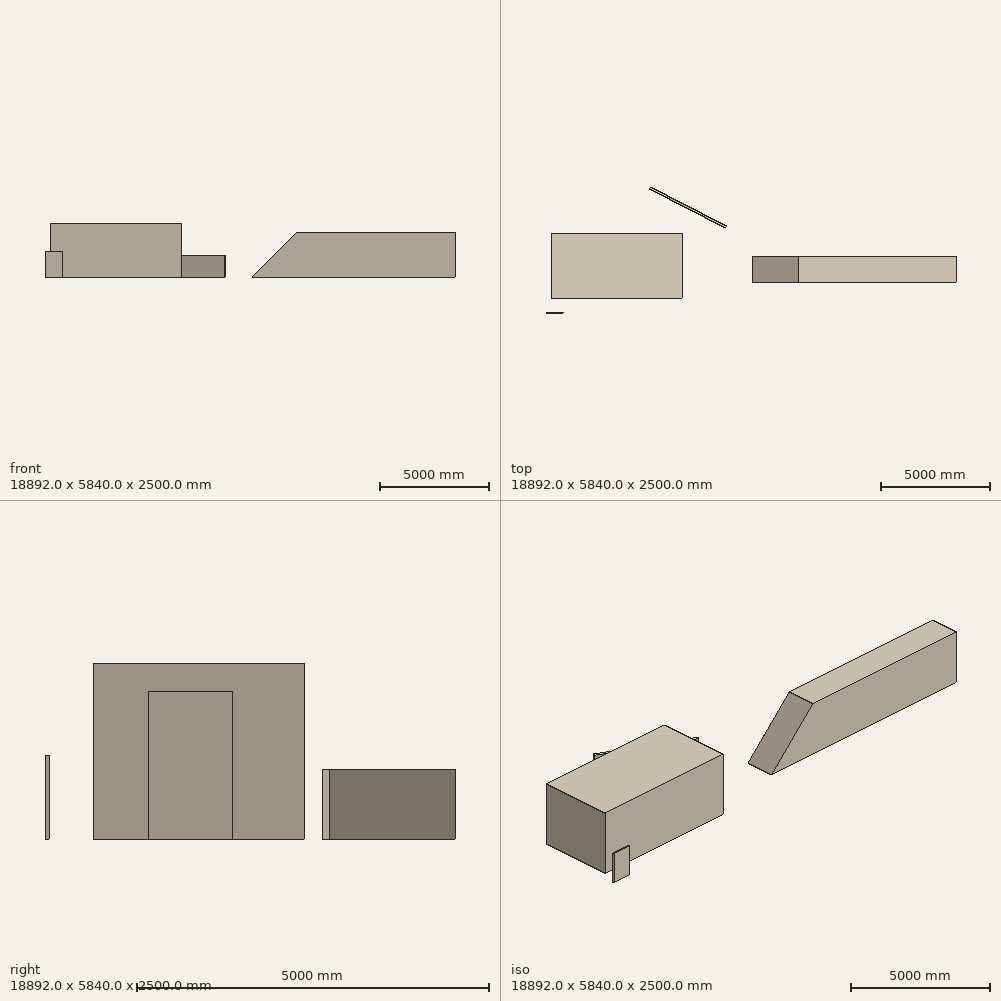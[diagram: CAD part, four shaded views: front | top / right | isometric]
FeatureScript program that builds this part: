
annotation { "Feature Type Name" : "Feature", "Feature Type Description" : "" }
export const myFeature = defineFeature(function(context is Context, id is Id, definition is map)
    precondition{}
    {
        {
            var Q0;
            Q0=qCreatedBy(makeId("Top.planeOp"),FACE);
            var sketch = newSketch(context, id + "F0", { "sketchPlane" : qUnion([Q0])});
            skLineSegment(sketch, "E0.bottom", {"start": v(-3001.21, 1533.07) * mm, "end": v(2998.79, 1533.07) * mm});
            skLineSegment(sketch, "E0.top", {"start": v(-3001.21, -1466.93) * mm, "end": v(2998.79, -1466.93) * mm});
            skLineSegment(sketch, "E0.left", {"start": v(-3001.21, 1533.07) * mm, "end": v(-3001.21, -1466.93) * mm});
            skLineSegment(sketch, "E0.right", {"start": v(2998.79, 1533.07) * mm, "end": v(2998.79, -1466.93) * mm});
            skSolve(sketch);
        }
        {
            var Q0;
            Q0=makeQuery(id+"F0.imprint","IMPRINT",FACE,{"disambiguationData":[TD([[makeQuery(id+"F0.imprint","IMPRINT",EDGE,{"derivedFrom":sQuery(id+"F0.wireOp",EDGE,"E0.bottom")}),-1.0]])]});
            extrude(context, id + "F1", {"entities" : qUnion([Q0]), "depth" : 2500 * mm, "offsetDistance" : 25 * mm});
        }
        {
            var Q0;
            Q0=qCreatedBy(makeId("Top.planeOp"),FACE);
            var sketch = newSketch(context, id + "F2", { "sketchPlane" : qUnion([Q0])});
            skLineSegment(sketch, "E1.bottom", {"start": v(8340.27, 507.97) * mm, "end": v(15640.27, 507.97) * mm});
            skLineSegment(sketch, "E1.top", {"start": v(8340.27, -692.03) * mm, "end": v(15640.27, -692.03) * mm});
            skLineSegment(sketch, "E1.left", {"start": v(8340.27, 507.97) * mm, "end": v(8340.27, -692.03) * mm});
            skLineSegment(sketch, "E1.right", {"start": v(15640.27, 507.97) * mm, "end": v(15640.27, -692.03) * mm});
            skSolve(sketch);
        }
        {
            var Q0;
            Q0=makeQuery(id+"F2.imprint","IMPRINT",FACE,{"disambiguationData":[TD([[makeQuery(id+"F2.imprint","IMPRINT",EDGE,{"derivedFrom":sQuery(id+"F2.wireOp",EDGE,"E1.bottom")}),-1.0]])]});
            extrude(context, id + "F3", {"entities" : qUnion([Q0]), "depth" : 2100 * mm, "offsetDistance" : 25 * mm});
        }
        {
            var Q0;
            Q0=makeQuery(id+"F3.opExtrude","SWEPT_FACE",FACE,{"disambiguationData":[OSD([sQuery(id+"F2.wireOp",EDGE,"E1.top")])]});
            var sketch = newSketch(context, id + "F4", { "sketchPlane" : qUnion([Q0])});
            skLineSegment(sketch, "E2", {"start": v(8340.27, 0) * mm, "end": v(6240.27, 0) * mm});
            skLineSegment(sketch, "E3", {"start": v(6240.27, 0) * mm, "end": v(8340.27, 2100) * mm});
            skSolve(sketch);
        }
        {
            var Q0;
            Q0=makeQuery(id+"F4.imprint","IMPRINT",FACE,{"disambiguationData":[TD([[makeQuery(id+"F4.imprint","IMPRINT",EDGE,{"derivedFrom":sQuery(id+"F4.wireOp",EDGE,"E2")}),-1.0]])]});
            var Q1;
            Q1=makeQuery(id+"F3.opExtrude","SWEPT_FACE",FACE,{"disambiguationData":[OSD([sQuery(id+"F2.wireOp",EDGE,"E1.bottom")])]});
            extrude(context, id + "F5", {"entities" : qUnion([Q0]), "operationType" : NewBodyOperationType.ADD, "endBound" : BoundingType.UP_TO_SURFACE, "oppositeDirection" : true, "depth" : 25 * mm, "endBoundEntityFace" : qUnion([Q1]), "offsetDistance" : 25 * mm});
        }
        {
            var Q0;
            Q0=qCreatedBy(makeId("Top.planeOp"),FACE);
            var sketch = newSketch(context, id + "F6", { "sketchPlane" : qUnion([Q0])});
            skLineSegment(sketch, "E4", {"start": v(1549.63, 3682.95) * mm, "end": v(5049.63, 1882.95) * mm});
            skLineSegment(sketch, "E5.0", {"start": v(1503.9, 3594.02) * mm, "end": v(5003.9, 1794.02) * mm});
            skLineSegment(sketch, "E6", {"start": v(1503.9, 3594.02) * mm, "end": v(1549.63, 3682.95) * mm});
            skLineSegment(sketch, "E7", {"start": v(5049.63, 1882.95) * mm, "end": v(5003.9, 1794.02) * mm});
            skLineSegment(sketch, "E8.bottom", {"start": v(363.52, -2093.9) * mm, "end": v(1163.52, -2093.9) * mm});
            skLineSegment(sketch, "E8.top", {"start": v(363.52, -2153.9) * mm, "end": v(1163.52, -2153.9) * mm});
            skLineSegment(sketch, "E8.left", {"start": v(363.52, -2093.9) * mm, "end": v(363.52, -2153.9) * mm});
            skLineSegment(sketch, "E8.right", {"start": v(1163.52, -2093.9) * mm, "end": v(1163.52, -2153.9) * mm});
            skSolve(sketch);
        }
        {
            var Q0;
            Q0=makeQuery(id+"F6.imprint","IMPRINT",FACE,{"disambiguationData":[TD([[makeQuery(id+"F6.imprint","IMPRINT",EDGE,{"derivedFrom":sQuery(id+"F6.wireOp",EDGE,"E4")}),-1.0]])]});
            extrude(context, id + "F7", {"entities" : qUnion([Q0]), "depth" : 1000 * mm, "offsetDistance" : 25 * mm});
        }
        {
            var Q0;
            Q0=qCreatedBy(makeId("Top.planeOp"),FACE);
            var sketch = newSketch(context, id + "F8", { "sketchPlane" : qUnion([Q0])});
            skLineSegment(sketch, "E9.bottom", {"start": v(-3251.73, -2097.01) * mm, "end": v(-2451.73, -2097.01) * mm});
            skLineSegment(sketch, "E9.top", {"start": v(-3251.73, -2157.01) * mm, "end": v(-2451.73, -2157.01) * mm});
            skLineSegment(sketch, "E9.left", {"start": v(-3251.73, -2097.01) * mm, "end": v(-3251.73, -2157.01) * mm});
            skLineSegment(sketch, "E9.right", {"start": v(-2451.73, -2097.01) * mm, "end": v(-2451.73, -2157.01) * mm});
            skSolve(sketch);
        }
        {
            var Q0;
            Q0=makeQuery(id+"F8.imprint","IMPRINT",FACE,{"disambiguationData":[TD([[makeQuery(id+"F8.imprint","IMPRINT",EDGE,{"derivedFrom":sQuery(id+"F8.wireOp",EDGE,"E9.bottom")}),-1.0]])]});
            extrude(context, id + "F9", {"entities" : qUnion([Q0]), "depth" : 1200 * mm, "offsetDistance" : 25 * mm});
        }
    });
